# Revit family: 1811-pendant-1M
name_source: partatom
category: Lighting Fixtures
revit_build: Autodesk Revit 2017 (Build: 20160225_1515(x64)
units: mm (PartAtom-declared; Revit-internal decimal feet)

## family parameters
Always vertical = Yes
Cut with Voids When Loaded = No
Host = Ceiling
Light Source = No
OmniClass Number = 23.80.70.11
OmniClass Title = Luminaries for Internal Lighting
Part Type = Normal
Room Calculation Point = No
Round Connector Dimension = Use Diameter
Shared = No

## types (2) — shared parameters
Body Material = Aluminum
Flicker = Free Flicker
Height = 6 cm
IP = 4X
Lamp = LED
Length = 100 cm
Manufacturer = SHOA
Model = SH-1811Pendant
Protection Class = class I
Type medule = SMD-DOB
URL = https://www.shoaco.com
Voltage/Frequency = 230V/50HZ
Website = www.shoaco.com
Width = 10 cm
color rendering index(CRI) = 80
color temperature = 4000K
consumption current = 0 A
instalation = Pendant Mounted
wattage. = 50 W

## per-type parameters (varying)
| type | Body color |
| SH-1811-Pendant(Black Body-4000K-LED-100cm) | Black Body |
| SH-1811-Pendant(White Body-4000K-LED-100cm) | White Body |

## geometry (parser evidence)
native form markers: Sweep x4
no freeform markers — native parametric forms only
